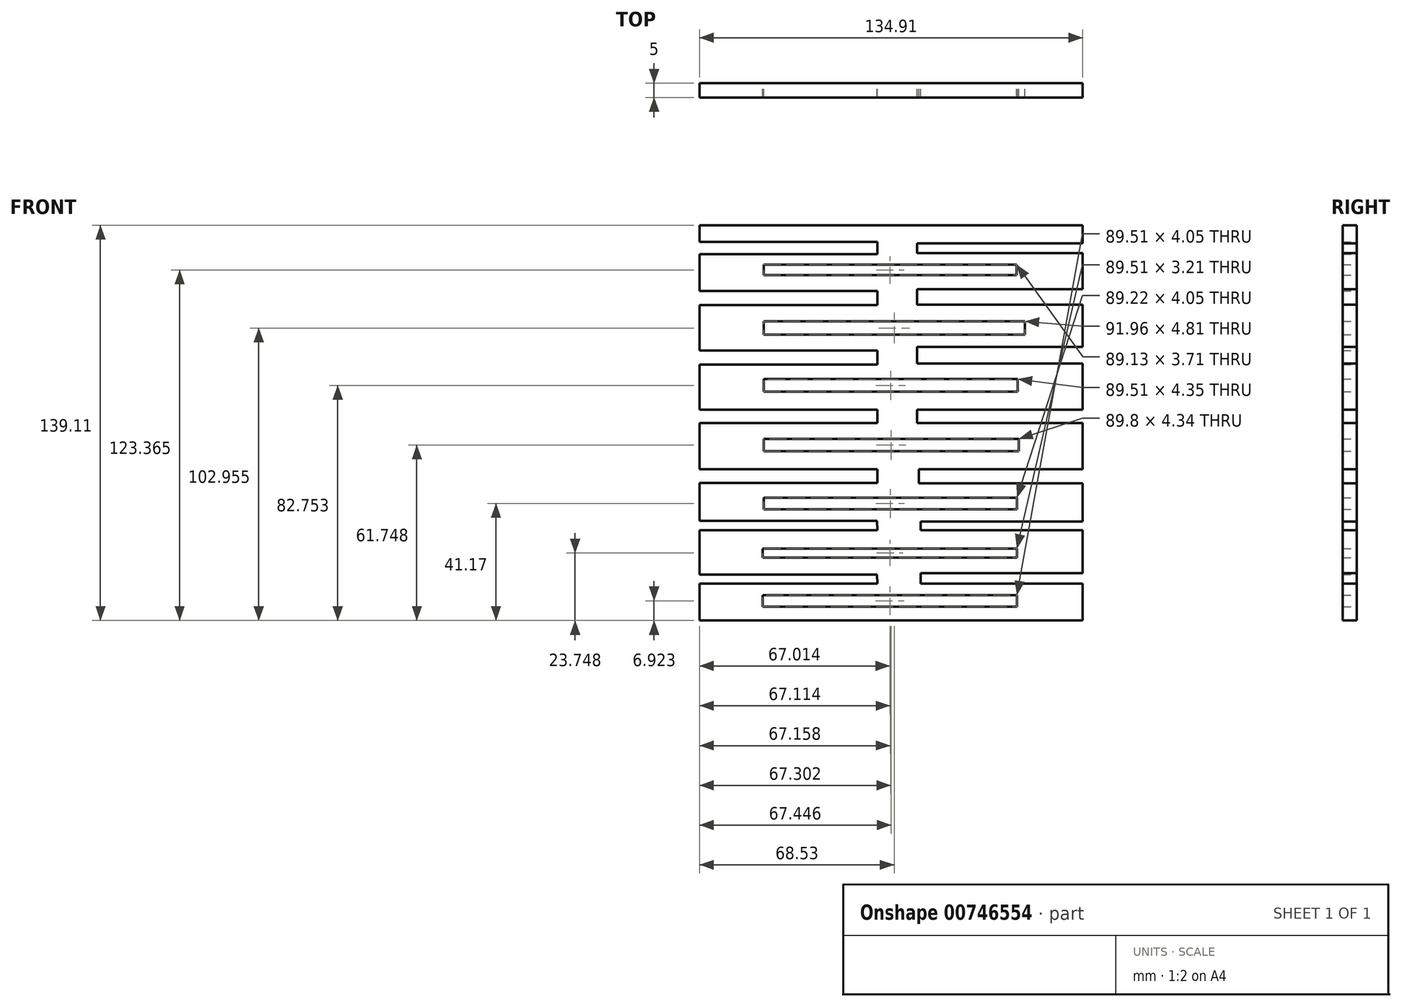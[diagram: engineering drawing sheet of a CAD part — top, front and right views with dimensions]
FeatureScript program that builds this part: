
annotation { "Feature Type Name" : "Feature", "Feature Type Description" : "" }
export const myFeature = defineFeature(function(context is Context, id is Id, definition is map)
    precondition{}
    {
        {
            var Q0;
            Q0=qCreatedBy(makeId("Front.planeOp"),FACE);
            var sketch = newSketch(context, id + "F0", { "sketchPlane" : qUnion([Q0])});
            skLineSegment(sketch, "E0.bottom", {"start": v(-70.18, 69.58) * mm, "end": v(64.73, 69.58) * mm});
            skLineSegment(sketch, "E0.top", {"start": v(-70.18, -69.53) * mm, "end": v(64.73, -69.53) * mm});
            skLineSegment(sketch, "E0.left", {"start": v(-70.18, 69.58) * mm, "end": v(-70.18, 63.75) * mm});
            skLineSegment(sketch, "E0.right", {"start": v(64.73, 69.58) * mm, "end": v(64.73, 63.17) * mm});
            skLineSegment(sketch, "E1.bottom", {"start": v(-47.92, -60.58) * mm, "end": v(41.59, -60.58) * mm});
            skLineSegment(sketch, "E1.top", {"start": v(-47.92, -64.63) * mm, "end": v(41.59, -64.63) * mm});
            skLineSegment(sketch, "E1.left", {"start": v(-47.92, -60.58) * mm, "end": v(-47.92, -64.63) * mm});
            skLineSegment(sketch, "E1.right", {"start": v(41.59, -60.58) * mm, "end": v(41.59, -64.63) * mm});
            skLineSegment(sketch, "E2.bottom", {"start": v(-70.18, -53.39) * mm, "end": v(-7.63, -53.39) * mm});
            skLineSegment(sketch, "E2.top", {"start": v(-70.18, -56.51) * mm, "end": v(-7.5, -56.51) * mm});
            skLineSegment(sketch, "E2.right", {"start": v(-7.63, -53.39) * mm, "end": v(-7.5, -56.51) * mm});
            skLineSegment(sketch, "E3.bottom", {"start": v(64.73, -52.81) * mm, "end": v(7.63, -52.81) * mm});
            skLineSegment(sketch, "E3.top", {"start": v(64.73, -56.51) * mm, "end": v(7.63, -56.51) * mm});
            skLineSegment(sketch, "E3.right", {"start": v(7.63, -52.81) * mm, "end": v(7.63, -56.51) * mm});
            skLineSegment(sketch, "E4.bottom", {"start": v(-47.92, -44.18) * mm, "end": v(41.59, -44.18) * mm});
            skLineSegment(sketch, "E4.top", {"start": v(-47.92, -47.38) * mm, "end": v(41.59, -47.38) * mm});
            skLineSegment(sketch, "E4.left", {"start": v(-47.92, -44.18) * mm, "end": v(-47.92, -47.38) * mm});
            skLineSegment(sketch, "E4.right", {"start": v(41.59, -44.18) * mm, "end": v(41.59, -47.38) * mm});
            skLineSegment(sketch, "E5.bottom", {"start": v(-70.18, -34.4) * mm, "end": v(-7.63, -34.4) * mm});
            skLineSegment(sketch, "E5.top", {"start": v(-70.18, -37.82) * mm, "end": v(-7.5, -37.82) * mm});
            skLineSegment(sketch, "E5.right", {"start": v(-7.63, -34.4) * mm, "end": v(-7.5, -37.82) * mm});
            skLineSegment(sketch, "E6.bottom", {"start": v(64.73, -34.68) * mm, "end": v(7.63, -34.68) * mm});
            skLineSegment(sketch, "E6.top", {"start": v(64.73, -37.82) * mm, "end": v(7.63, -37.82) * mm});
            skLineSegment(sketch, "E6.right", {"start": v(7.63, -34.68) * mm, "end": v(7.63, -37.82) * mm});
            skLineSegment(sketch, "E7.bottom", {"start": v(-47.63, -26.33) * mm, "end": v(41.59, -26.33) * mm});
            skLineSegment(sketch, "E7.top", {"start": v(-47.63, -30.39) * mm, "end": v(41.59, -30.39) * mm});
            skLineSegment(sketch, "E7.left", {"start": v(-47.63, -26.33) * mm, "end": v(-47.63, -30.39) * mm});
            skLineSegment(sketch, "E7.right", {"start": v(41.59, -26.33) * mm, "end": v(41.59, -30.39) * mm});
            skLineSegment(sketch, "E8.bottom", {"start": v(-70.18, -16.29) * mm, "end": v(-7.5, -16.29) * mm});
            skLineSegment(sketch, "E8.top", {"start": v(-70.18, -21.1) * mm, "end": v(-7.5, -21.1) * mm});
            skLineSegment(sketch, "E8.right", {"start": v(-7.5, -16.29) * mm, "end": v(-7.5, -21.1) * mm});
            skLineSegment(sketch, "E9.bottom", {"start": v(7.05, -16.29) * mm, "end": v(64.73, -16.29) * mm});
            skLineSegment(sketch, "E9.top", {"start": v(7.05, -21.19) * mm, "end": v(64.73, -21.19) * mm});
            skLineSegment(sketch, "E9.left", {"start": v(7.05, -16.29) * mm, "end": v(7.05, -21.19) * mm});
            skLineSegment(sketch, "E10.bottom", {"start": v(-47.63, -9.95) * mm, "end": v(42.16, -9.95) * mm});
            skLineSegment(sketch, "E10.top", {"start": v(-47.63, -5.61) * mm, "end": v(42.16, -5.61) * mm});
            skLineSegment(sketch, "E10.left", {"start": v(-47.63, -9.95) * mm, "end": v(-47.63, -5.61) * mm});
            skLineSegment(sketch, "E10.right", {"start": v(42.16, -9.95) * mm, "end": v(42.16, -5.61) * mm});
            skLineSegment(sketch, "E11.bottom", {"start": v(-70.18, 0) * mm, "end": v(-7.6, 0) * mm});
            skLineSegment(sketch, "E11.top", {"start": v(-70.18, 4.67) * mm, "end": v(-7.5, 4.67) * mm});
            skLineSegment(sketch, "E11.right", {"start": v(-7.6, 0) * mm, "end": v(-7.5, 4.67) * mm});
            skLineSegment(sketch, "E12.bottom", {"start": v(6.48, 4.67) * mm, "end": v(64.73, 4.67) * mm});
            skLineSegment(sketch, "E12.top", {"start": v(6.48, 0) * mm, "end": v(64.73, 0) * mm});
            skLineSegment(sketch, "E12.left", {"start": v(6.48, 4.67) * mm, "end": v(6.48, 0) * mm});
            skLineSegment(sketch, "E13.bottom", {"start": v(-47.63, 11.05) * mm, "end": v(41.88, 11.05) * mm});
            skLineSegment(sketch, "E13.top", {"start": v(-47.63, 15.4) * mm, "end": v(41.88, 15.4) * mm});
            skLineSegment(sketch, "E13.left", {"start": v(-47.63, 11.05) * mm, "end": v(-47.63, 15.4) * mm});
            skLineSegment(sketch, "E13.right", {"start": v(41.88, 11.05) * mm, "end": v(41.88, 15.4) * mm});
            skLineSegment(sketch, "E14.bottom", {"start": v(-7.5, 20.56) * mm, "end": v(-70.18, 20.56) * mm});
            skLineSegment(sketch, "E14.top", {"start": v(-7.5, 25.47) * mm, "end": v(-70.18, 25.47) * mm});
            skLineSegment(sketch, "E14.left", {"start": v(-7.5, 20.56) * mm, "end": v(-7.5, 25.47) * mm});
            skLineSegment(sketch, "E15.bottom", {"start": v(6.48, 20.9) * mm, "end": v(64.73, 20.9) * mm});
            skLineSegment(sketch, "E15.top", {"start": v(6.48, 26.77) * mm, "end": v(64.73, 26.77) * mm});
            skLineSegment(sketch, "E15.left", {"start": v(6.48, 20.9) * mm, "end": v(6.48, 26.77) * mm});
            skLineSegment(sketch, "E16.bottom", {"start": v(-7.5, 41.5) * mm, "end": v(-70.18, 41.5) * mm});
            skLineSegment(sketch, "E16.top", {"start": v(-7.5, 46.48) * mm, "end": v(-70.18, 46.48) * mm});
            skLineSegment(sketch, "E16.left", {"start": v(-7.5, 41.5) * mm, "end": v(-7.5, 46.48) * mm});
            skLineSegment(sketch, "E17.bottom", {"start": v(6.48, 41.57) * mm, "end": v(64.73, 41.57) * mm});
            skLineSegment(sketch, "E17.top", {"start": v(6.48, 47.06) * mm, "end": v(64.73, 47.06) * mm});
            skLineSegment(sketch, "E17.left", {"start": v(6.48, 41.57) * mm, "end": v(6.48, 47.06) * mm});
            skLineSegment(sketch, "E18.bottom", {"start": v(-47.63, 51.98) * mm, "end": v(41.5, 51.98) * mm});
            skLineSegment(sketch, "E18.top", {"start": v(-47.63, 55.7) * mm, "end": v(41.5, 55.7) * mm});
            skLineSegment(sketch, "E18.left", {"start": v(-47.63, 51.98) * mm, "end": v(-47.63, 55.7) * mm});
            skLineSegment(sketch, "E18.right", {"start": v(41.5, 51.98) * mm, "end": v(41.5, 55.7) * mm});
            skLineSegment(sketch, "E19.bottom", {"start": v(-7.5, 59.43) * mm, "end": v(-70.18, 59.43) * mm});
            skLineSegment(sketch, "E19.top", {"start": v(-7.5, 63.75) * mm, "end": v(-70.18, 63.75) * mm});
            skLineSegment(sketch, "E19.left", {"start": v(-7.5, 59.43) * mm, "end": v(-7.5, 63.75) * mm});
            skLineSegment(sketch, "E20.bottom", {"start": v(6.48, 59.72) * mm, "end": v(64.73, 59.72) * mm});
            skLineSegment(sketch, "E20.top", {"start": v(6.48, 63.17) * mm, "end": v(64.73, 63.17) * mm});
            skLineSegment(sketch, "E20.left", {"start": v(6.48, 59.72) * mm, "end": v(6.48, 63.17) * mm});
            skLineSegment(sketch, "E21.trimOffspring", {"start": v(-70.18, 59.43) * mm, "end": v(-70.18, 46.48) * mm});
            skLineSegment(sketch, "E22.trimOffspring", {"start": v(-70.18, 41.5) * mm, "end": v(-70.18, 25.47) * mm});
            skLineSegment(sketch, "E23.trimOffspring", {"start": v(-70.18, 20.56) * mm, "end": v(-70.18, 4.67) * mm});
            skLineSegment(sketch, "E24.trimOffspring", {"start": v(-70.18, 0) * mm, "end": v(-70.18, -16.29) * mm});
            skLineSegment(sketch, "E25.trimOffspring", {"start": v(-70.18, -21.1) * mm, "end": v(-70.18, -34.4) * mm});
            skLineSegment(sketch, "E26.trimOffspring", {"start": v(-70.18, -37.82) * mm, "end": v(-70.18, -53.39) * mm});
            skLineSegment(sketch, "E27.trimOffspring", {"start": v(-70.18, -56.51) * mm, "end": v(-70.18, -69.53) * mm});
            skLineSegment(sketch, "E28.trimOffspring", {"start": v(64.73, -56.51) * mm, "end": v(64.73, -69.53) * mm});
            skLineSegment(sketch, "E29.trimOffspring", {"start": v(64.73, -37.82) * mm, "end": v(64.73, -52.81) * mm});
            skLineSegment(sketch, "E30.trimOffspring", {"start": v(64.73, -21.19) * mm, "end": v(64.73, -34.68) * mm});
            skLineSegment(sketch, "E31.trimOffspring", {"start": v(64.73, 0) * mm, "end": v(64.73, -16.29) * mm});
            skLineSegment(sketch, "E32.trimOffspring", {"start": v(64.73, 20.9) * mm, "end": v(64.73, 4.67) * mm});
            skLineSegment(sketch, "E33.trimOffspring", {"start": v(64.73, 41.57) * mm, "end": v(64.73, 26.77) * mm});
            skLineSegment(sketch, "E34.trimOffspring", {"start": v(64.73, 59.72) * mm, "end": v(64.73, 47.06) * mm});
            skPoint(sketch, "E35.left.end.orphan", {"position": v(-47.63, 35.83) * mm});
            skPoint(sketch, "E35.left.start.orphan", {"position": v(-47.63, 30.65) * mm});
            skLineSegment(sketch, "E36.bottom", {"start": v(-47.63, 35.83) * mm, "end": v(44.33, 35.83) * mm});
            skLineSegment(sketch, "E36.top", {"start": v(-47.63, 31.02) * mm, "end": v(44.33, 31.02) * mm});
            skLineSegment(sketch, "E36.left", {"start": v(-47.63, 35.83) * mm, "end": v(-47.63, 31.02) * mm});
            skLineSegment(sketch, "E36.right", {"start": v(44.33, 35.83) * mm, "end": v(44.33, 31.02) * mm});
            skSolve(sketch);
        }
        {
            var Q0;
            Q0=makeQuery(id+"F0.imprint","IMPRINT",FACE,{"disambiguationData":[TD([[makeQuery(id+"F0.imprint","IMPRINT",EDGE,{"derivedFrom":sQuery(id+"F0.wireOp",EDGE,"E0.bottom")}),-1.0]])]});
            extrude(context, id + "F1", {"entities" : qUnion([Q0]), "depth" : 5 * mm, "offsetDistance" : 25 * mm});
        }
    });
